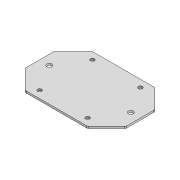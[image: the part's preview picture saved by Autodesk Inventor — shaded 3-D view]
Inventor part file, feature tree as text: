
AUTODESK INVENTOR PART (.ipt)
format: ipt  version: 2020 (Build 240168000, 168)  size: 136,704 bytes
history: native  units: mm
features: sketch x4, extrude x2, hole x2, other x1, chamfer x1, fillet x1
ambient origin geometry x8: Origin, YZ Plane, XZ Plane, XY Plane, X Axis, Y Axis, Z Axis, Center Point
bodies: Body1 (feature_tree)
feature tree (11):
  other  "ソリッド1"
  extrude  "押し出し1"  Depth=65.0mm
  hole  "穴1"  [1 undecoded]
  extrude  "押し出し3"  Depth=2.0mm TaperAngle=0.0deg
  chamfer  "面取り3"  Distance=50.0mm
  hole  "穴4"  [1 undecoded]
  fillet  "フィレット4"  Radius=20.0mm
  sketch  "スケッチ1"
  sketch  "スケッチ2"
  sketch  "スケッチ6"
  sketch  "スケッチ7"
note: 2 required parameter values undecoded (feature->parameter linkage not recoverable at this tier; creation-order binding heuristic only, values carry confidence <= 0.55)
